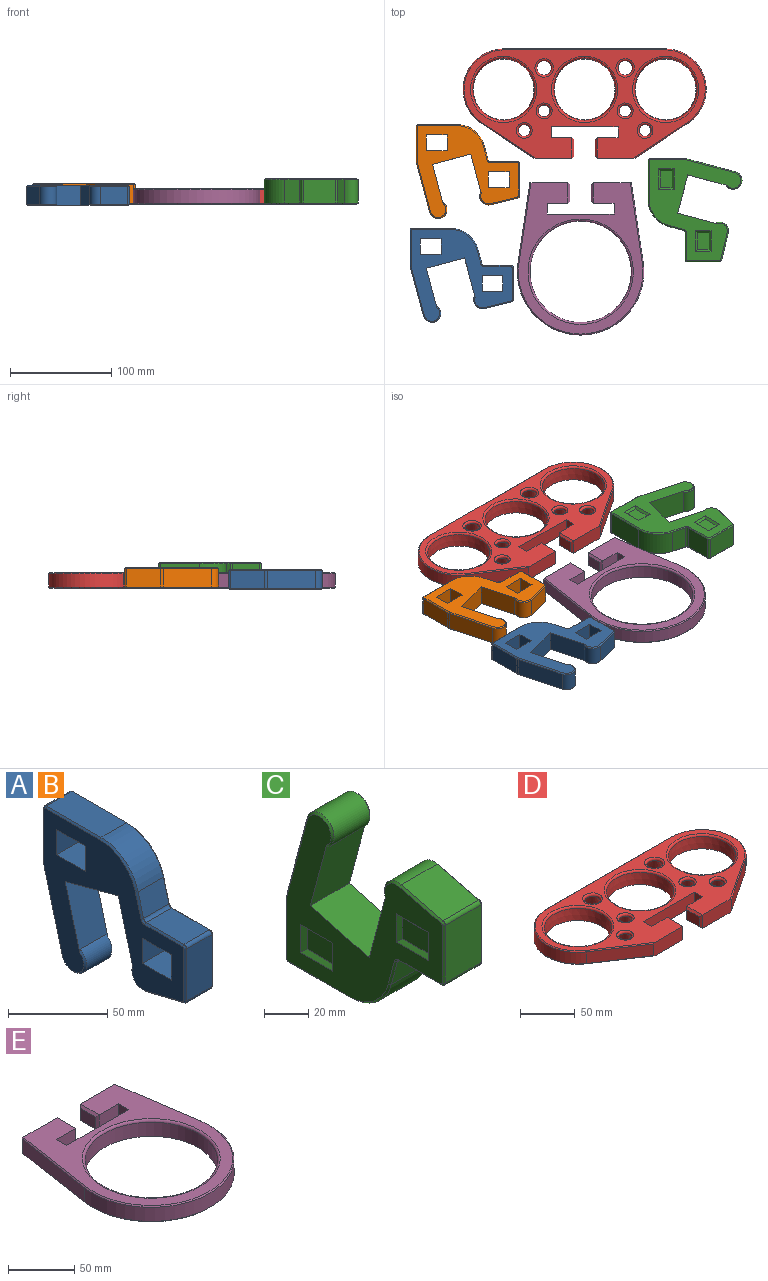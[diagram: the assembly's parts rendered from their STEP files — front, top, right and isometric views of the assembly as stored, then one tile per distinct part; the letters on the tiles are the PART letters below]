
ASSEMBLY  parts=5 mates=3
PART A: 58 faces, bbox 20x101.8x92.6 mm
  f0: plane 99.77x90.57mm, normal (1,0,0), area 3782.3mm2, adj f1,f2,f3,f4,f5,f15,f16,f17
  f1: plane 20x15.6mm, normal (0,-1,0), area 312mm2, adj f0,f14,f15,f16
  f2: plane 20x15.6mm, normal (0,-1,0), area 312mm2, adj f0,f14,f21,f22
  f3: plane 38.64x20mm, normal (0,0.97,-0.26), area 770.8mm2, adj f0,f4,f14,f19,f42,f57
  f4: plane 37.77x20mm, normal (0,-0.26,-0.97), area 782mm2, adj f0,f3,f5,f14
  f5: plane 38.64x20mm, normal (0,-0.97,0.26), area 770.8mm2, adj f0,f4,f6,f14,f28,f43
  f6: cylinder r=8.75mm len=18mm, axis (-1,0,0), area 616.9mm2, adj f5,f7,f28,f43
  f7: plane 47.9x18mm, normal (0,0.97,-0.26), area 892.6mm2, adj f6,f8,f29,f44
  f8: cylinder r=10mm len=18mm, axis (-1,0,0), area 47.1mm2, adj f7,f9,f30,f45
  f9: plane 33.6x18mm, normal (0,1,0), area 604.8mm2, adj f8,f24,f31,f46
  f10: plane 38.63x18mm, normal (0,0,1), area 695.3mm2, adj f11,f24,f33,f48
  f11: cylinder r=27.39mm len=26.46mm, axis (-1,0,0), area 645.5mm2, adj f10,f12,f34,f49
  f12: plane 18x14.63mm, normal (0,-0.97,0.26), area 272.7mm2, adj f11,f25,f35,f50
  f13: plane 26.83x18mm, normal (0,0,1), area 482.9mm2, adj f25,f26,f37,f52
  f14: plane 99.77x90.57mm, normal (-1,0,0), area 3782.3mm2, adj f1,f2,f3,f4,f5,f15,f16,f17
  f15: plane 20.6x20mm, normal (0,0,1), area 412mm2, adj f0,f1,f14,f17
  f16: plane 20.6x20mm, normal (0,0,-1), area 412mm2, adj f0,f1,f14,f17
  f17: plane 20x15.6mm, normal (0,1,0), area 312mm2, adj f0,f14,f15,f16
  f18: plane 32.03x18mm, normal (0,-1,0), area 576.6mm2, adj f26,f27,f39,f54
  f19: cylinder r=8.75mm len=18mm, axis (-1,0,0), area 366.3mm2, adj f3,f20,f42,f57
  f20: plane 26.69x18mm, normal (0,-0.24,-0.97), area 494.7mm2, adj f19,f27,f41,f56
  f21: plane 20.6x20mm, normal (0,0,1), area 412mm2, adj f0,f2,f14,f23
  f22: plane 20.6x20mm, normal (0,0,-1), area 412mm2, adj f0,f2,f14,f23
  f23: plane 20x15.6mm, normal (0,1,0), area 312mm2, adj f0,f14,f21,f22
  f24: cylinder r=2mm len=18mm, axis (-1,0,0), area 56.5mm2, adj f9,f10,f32,f47
  f25: cylinder r=2mm len=18mm, axis (1,0,0), area 47.1mm2, adj f12,f13,f36,f51
  f26: cylinder r=2mm len=18mm, axis (-1,0,0), area 56.5mm2, adj f13,f18,f38,f53
  f27: cylinder r=2mm len=18mm, axis (-1,0,0), area 47.9mm2, adj f18,f20,f40,f55
  f28: cone r=8.75mm half-angle=45deg, axis (1,0,0), area 44.9mm2, adj f5,f6,f14,f29
  f29: plane 48.16x13.8mm, normal (-0.71,0.68,-0.18), area 70.1mm2, adj f7,f14,f28,f30
  f30: cone r=10mm half-angle=45deg, axis (1,0,0), area 3.5mm2, adj f8,f14,f29,f31
  f31: plane 33.6x1mm, normal (-0.71,0.71,0), area 47.5mm2, adj f9,f14,f30,f32
  f32: cone r=1mm half-angle=45deg, axis (1,0,0), area 3.3mm2, adj f14,f24,f31,f33
  f33: plane 38.63x1mm, normal (-0.71,0,0.71), area 54.6mm2, adj f10,f14,f32,f34
  f34: cone r=27.39mm half-angle=45deg, axis (1,0,0), area 49.8mm2, adj f11,f14,f33,f35
  f35: plane 14.89x4.89mm, normal (-0.71,-0.68,0.18), area 21.4mm2, adj f12,f14,f34,f36
  f36: cone r=3mm half-angle=45deg, axis (-1,0,0), area 4.6mm2, adj f14,f25,f35,f37
  f37: plane 26.83x1mm, normal (-0.71,0,0.71), area 37.9mm2, adj f13,f14,f36,f38
  f38: cone r=1mm half-angle=45deg, axis (1,0,0), area 3.3mm2, adj f14,f26,f37,f39
  f39: plane 32.03x1mm, normal (-0.71,-0.71,0), area 45.3mm2, adj f14,f18,f38,f40
  f40: cone r=1mm half-angle=45deg, axis (1,0,0), area 2.8mm2, adj f14,f27,f39,f41
  f41: plane 26.93x7.54mm, normal (-0.71,-0.17,-0.69), area 38.9mm2, adj f14,f20,f40,f42
  f42: cone r=8.75mm half-angle=45deg, axis (1,0,0), area 26.4mm2, adj f3,f14,f19,f41
  f43: cone r=7.75mm half-angle=45deg, axis (-1,0,0), area 44.9mm2, adj f0,f5,f6,f44
  f44: plane 48.16x13.8mm, normal (0.71,0.68,-0.18), area 70.1mm2, adj f0,f7,f43,f45
  f45: cone r=9mm half-angle=45deg, axis (-1,0,0), area 3.5mm2, adj f0,f8,f44,f46
  f46: plane 33.6x1mm, normal (0.71,0.71,0), area 47.5mm2, adj f0,f9,f45,f47
  f47: cone r=1mm half-angle=45deg, axis (-1,0,0), area 3.3mm2, adj f0,f24,f46,f48
  f48: plane 38.63x1mm, normal (0.71,0,0.71), area 54.6mm2, adj f0,f10,f47,f49
  f49: cone r=26.39mm half-angle=45deg, axis (-1,0,0), area 49.8mm2, adj f0,f11,f48,f50
  f50: plane 14.89x4.89mm, normal (0.71,-0.68,0.18), area 21.4mm2, adj f0,f12,f49,f51
  f51: cone r=3mm half-angle=45deg, axis (1,0,0), area 4.6mm2, adj f0,f25,f50,f52
  f52: plane 26.83x1mm, normal (0.71,0,0.71), area 37.9mm2, adj f0,f13,f51,f53
  f53: cone r=1mm half-angle=45deg, axis (-1,0,0), area 3.3mm2, adj f0,f26,f52,f54
  f54: plane 32.03x1mm, normal (0.71,-0.71,0), area 45.3mm2, adj f0,f18,f53,f55
  f55: cone r=1mm half-angle=45deg, axis (-1,0,0), area 2.8mm2, adj f0,f27,f54,f56
  f56: plane 26.93x7.54mm, normal (0.71,-0.17,-0.69), area 38.9mm2, adj f0,f20,f55,f57
  f57: cone r=7.75mm half-angle=45deg, axis (-1,0,0), area 26.4mm2, adj f0,f3,f19,f56
PART B: same geometry as A
PART C: 70 faces, bbox 25x101.8x92.6 mm
  f0: plane 99.77x90.57mm, normal (-1,0,0), area 3782.3mm2, adj f1,f2,f8,f20,f21,f22,f23,f24
  f1: plane 37.77x25mm, normal (0,-0.26,0.97), area 977.5mm2, adj f0,f2,f8,f12
  f2: plane 38.64x25mm, normal (0,0.97,0.26), area 963.1mm2, adj f0,f1,f3,f12,f54,f69
  f3: cylinder r=8.75mm len=23mm, axis (1,0,0), area 468mm2, adj f2,f4,f54,f69
  f4: plane 26.69x23mm, normal (0,-0.24,0.97), area 632.1mm2, adj f3,f36,f53,f68
  f5: plane 32.03x23mm, normal (0,-1,0), area 736.8mm2, adj f36,f37,f51,f66
  f6: plane 26.83x23mm, normal (0,0,-1), area 617.1mm2, adj f37,f38,f49,f64
  f7: plane 23x14.63mm, normal (0,-0.97,-0.26), area 348.4mm2, adj f9,f38,f47,f62
  f8: plane 38.64x25mm, normal (0,-0.97,-0.26), area 963.1mm2, adj f0,f1,f11,f12,f40,f55
  f9: cylinder r=27.39mm len=26.46mm, axis (1,0,0), area 824.7mm2, adj f7,f10,f46,f61
  f10: plane 38.63x23mm, normal (0,0,-1), area 888.4mm2, adj f9,f39,f45,f60
  f11: cylinder r=8.75mm len=23mm, axis (1,0,0), area 788.3mm2, adj f8,f13,f40,f55
  f12: plane 99.77x90.57mm, normal (1,0,0), area 3782.3mm2, adj f1,f2,f8,f28,f29,f30,f31,f32
  f13: plane 47.9x23mm, normal (0,0.97,0.26), area 1140.6mm2, adj f11,f15,f41,f56
  f14: plane 33.6x23mm, normal (0,1,0), area 772.8mm2, adj f15,f39,f43,f58
  f15: cylinder r=10mm len=23mm, axis (1,0,0), area 60.2mm2, adj f13,f14,f42,f57
  f16: plane 16.6x11.6mm, normal (-1,0,0), area 192.6mm2, adj f24,f25,f26,f27
  f17: plane 16.6x11.6mm, normal (1,0,0), area 192.6mm2, adj f32,f33,f34,f35
  f18: plane 16.6x11.6mm, normal (-1,0,0), area 192.6mm2, adj f20,f21,f22,f23
  f19: plane 16.6x11.6mm, normal (1,0,0), area 192.6mm2, adj f28,f29,f30,f31
  f20: plane 15.6x2mm, normal (-0.71,0.71,0), area 38.5mm2, adj f0,f18,f21,f22
  f21: plane 20.6x2mm, normal (-0.71,0,0.71), area 52.6mm2, adj f0,f18,f20,f23
  f22: plane 20.6x2mm, normal (-0.71,0,-0.71), area 52.6mm2, adj f0,f18,f20,f23
  f23: plane 15.6x2mm, normal (-0.71,-0.71,0), area 38.5mm2, adj f0,f18,f21,f22
  f24: plane 15.6x2mm, normal (-0.71,0.71,0), area 38.5mm2, adj f0,f16,f25,f26
  f25: plane 20.6x2mm, normal (-0.71,0,0.71), area 52.6mm2, adj f0,f16,f24,f27
  f26: plane 20.6x2mm, normal (-0.71,0,-0.71), area 52.6mm2, adj f0,f16,f24,f27
  f27: plane 15.6x2mm, normal (-0.71,-0.71,0), area 38.5mm2, adj f0,f16,f25,f26
  f28: plane 15.6x2mm, normal (0.71,0.71,0), area 38.5mm2, adj f12,f19,f29,f30
  f29: plane 20.6x2mm, normal (0.71,0,0.71), area 52.6mm2, adj f12,f19,f28,f31
  f30: plane 20.6x2mm, normal (0.71,0,-0.71), area 52.6mm2, adj f12,f19,f28,f31
  f31: plane 15.6x2mm, normal (0.71,-0.71,0), area 38.5mm2, adj f12,f19,f29,f30
  f32: plane 15.6x2mm, normal (0.71,0.71,0), area 38.5mm2, adj f12,f17,f33,f34
  f33: plane 20.6x2mm, normal (0.71,0,0.71), area 52.6mm2, adj f12,f17,f32,f35
  f34: plane 20.6x2mm, normal (0.71,0,-0.71), area 52.6mm2, adj f12,f17,f32,f35
  f35: plane 15.6x2mm, normal (0.71,-0.71,0), area 38.5mm2, adj f12,f17,f33,f34
  f36: cylinder r=2mm len=23mm, axis (1,0,0), area 61.2mm2, adj f4,f5,f52,f67
  f37: cylinder r=2mm len=23mm, axis (1,0,0), area 72.3mm2, adj f5,f6,f50,f65
  f38: cylinder r=2mm len=23mm, axis (-1,0,0), area 60.2mm2, adj f6,f7,f48,f63
  f39: cylinder r=2mm len=23mm, axis (1,0,0), area 72.3mm2, adj f10,f14,f44,f59
  f40: cone r=7.75mm half-angle=45deg, axis (1,0,0), area 44.9mm2, adj f0,f8,f11,f41
  f41: plane 48.16x13.8mm, normal (-0.71,0.68,0.18), area 70.1mm2, adj f0,f13,f40,f42
  f42: cone r=9mm half-angle=45deg, axis (1,0,0), area 3.5mm2, adj f0,f15,f41,f43
  f43: plane 33.6x1mm, normal (-0.71,0.71,0), area 47.5mm2, adj f0,f14,f42,f44
  f44: cone r=1mm half-angle=45deg, axis (1,0,0), area 3.3mm2, adj f0,f39,f43,f45
  f45: plane 38.63x1mm, normal (-0.71,0,-0.71), area 54.6mm2, adj f0,f10,f44,f46
  f46: cone r=26.39mm half-angle=45deg, axis (1,0,0), area 49.8mm2, adj f0,f9,f45,f47
  f47: plane 14.89x4.89mm, normal (-0.71,-0.68,-0.18), area 21.4mm2, adj f0,f7,f46,f48
  f48: cone r=3mm half-angle=45deg, axis (-1,0,0), area 4.6mm2, adj f0,f38,f47,f49
  f49: plane 26.83x1mm, normal (-0.71,0,-0.71), area 37.9mm2, adj f0,f6,f48,f50
  f50: cone r=1mm half-angle=45deg, axis (1,0,0), area 3.3mm2, adj f0,f37,f49,f51
  f51: plane 32.03x1mm, normal (-0.71,-0.71,0), area 45.3mm2, adj f0,f5,f50,f52
  f52: cone r=1mm half-angle=45deg, axis (1,0,0), area 2.8mm2, adj f0,f36,f51,f53
  f53: plane 26.93x7.54mm, normal (-0.71,-0.17,0.69), area 38.9mm2, adj f0,f4,f52,f54
  f54: cone r=7.75mm half-angle=45deg, axis (1,0,0), area 26.4mm2, adj f0,f2,f3,f53
  f55: cone r=8.75mm half-angle=45deg, axis (-1,0,0), area 44.9mm2, adj f8,f11,f12,f56
  f56: plane 48.16x13.8mm, normal (0.71,0.68,0.18), area 70.1mm2, adj f12,f13,f55,f57
  f57: cone r=10mm half-angle=45deg, axis (-1,0,0), area 3.5mm2, adj f12,f15,f56,f58
  f58: plane 33.6x1mm, normal (0.71,0.71,0), area 47.5mm2, adj f12,f14,f57,f59
  f59: cone r=1mm half-angle=45deg, axis (-1,0,0), area 3.3mm2, adj f12,f39,f58,f60
  f60: plane 38.63x1mm, normal (0.71,0,-0.71), area 54.6mm2, adj f10,f12,f59,f61
  f61: cone r=27.39mm half-angle=45deg, axis (-1,0,0), area 49.8mm2, adj f9,f12,f60,f62
  f62: plane 14.89x4.89mm, normal (0.71,-0.68,-0.18), area 21.4mm2, adj f7,f12,f61,f63
  f63: cone r=3mm half-angle=45deg, axis (1,0,0), area 4.6mm2, adj f12,f38,f62,f64
  f64: plane 26.83x1mm, normal (0.71,0,-0.71), area 37.9mm2, adj f6,f12,f63,f65
  f65: cone r=1mm half-angle=45deg, axis (-1,0,0), area 3.3mm2, adj f12,f37,f64,f66
  f66: plane 32.03x1mm, normal (0.71,-0.71,0), area 45.3mm2, adj f5,f12,f65,f67
  f67: cone r=1mm half-angle=45deg, axis (-1,0,0), area 2.8mm2, adj f12,f36,f66,f68
  f68: plane 26.93x7.54mm, normal (0.71,-0.17,0.69), area 38.9mm2, adj f4,f12,f67,f69
  f69: cone r=8.75mm half-angle=45deg, axis (-1,0,0), area 26.4mm2, adj f2,f3,f12,f68
PART D: 52 faces, bbox 240x107.8x15 mm
  f0: plane 238x106.8mm, normal (0,0,1), area 8736.8mm2, adj f2,f3,f4,f5,f6,f8,f10,f28
  f1: plane 16x11mm, normal (1,0,0), area 176mm2, adj f25,f26,f27,f28
  f2: plane 20.5x15mm, normal (0,1,0), area 307.5mm2, adj f0,f3,f13,f26
  f3: plane 15x10.8mm, normal (1,0,0), area 162mm2, adj f0,f2,f4,f13
  f4: plane 66x15mm, normal (0,-1,0), area 990mm2, adj f0,f3,f5,f13
  f5: plane 15x10.8mm, normal (-1,0,0), area 162mm2, adj f0,f4,f6,f13
  f6: plane 20.5x15mm, normal (0,1,0), area 307.5mm2, adj f0,f5,f13,f30
  f7: plane 16x11mm, normal (-1,0,0), area 176mm2, adj f29,f30,f31,f32
  f8: plane 37.5x15mm, normal (0,-1,0), area 560.7mm2, adj f0,f9,f13,f31,f46,f47
  f9: plane 52.07x34.44mm, normal (0.55,-0.83,0), area 811.5mm2, adj f8,f11,f46,f47
  f10: plane 37.5x15mm, normal (0,-1,0), area 560.7mm2, adj f0,f12,f13,f27,f42,f51
  f11: cylinder r=40mm len=73.36mm, axis (0,0,-1), area 1329.8mm2, adj f9,f23,f45,f48
  f12: plane 52.07x34.44mm, normal (-0.55,-0.83,0), area 811.5mm2, adj f10,f24,f42,f51
  f13: plane 238x106.8mm, normal (0,0,-1), area 9382.8mm2, adj f2,f3,f4,f5,f6,f8,f10,f14
  f14: cone r=30mm half-angle=3deg, axis (0,0,1), area 2501.9mm2, adj f13,f41
  f15: cone r=30mm half-angle=3deg, axis (0,0,1), area 2501.9mm2, adj f13,f40
  f16: cone r=30mm half-angle=3deg, axis (0,0,1), area 2501.9mm2, adj f13,f39
  f17: cone r=6.25mm half-angle=20deg, axis (0,0,-1), area 779.7mm2, adj f13,f38
  f18: cone r=5mm half-angle=20deg, axis (0,0,-1), area 676.8mm2, adj f13,f33
  f19: cone r=5mm half-angle=20deg, axis (0,0,-1), area 676.8mm2, adj f13,f37
  f20: cone r=5mm half-angle=20deg, axis (0,0,-1), area 676.8mm2, adj f13,f34
  f21: cone r=5mm half-angle=20deg, axis (0,0,-1), area 676.8mm2, adj f13,f36
  f22: cone r=6.25mm half-angle=20deg, axis (0,0,-1), area 779.7mm2, adj f13,f35
  f23: plane 160x13mm, normal (0,1,0), area 2080mm2, adj f11,f24,f44,f49
  f24: cylinder r=40mm len=73.36mm, axis (0,0,-1), area 1329.8mm2, adj f12,f23,f43,f50
  f25: plane 20x2mm, normal (0.71,0,-0.71), area 50.9mm2, adj f1,f13,f26,f27
  f26: plane 15x2mm, normal (0.71,0.71,0), area 36.8mm2, adj f1,f2,f25,f28
  f27: plane 15x2mm, normal (0.71,-0.71,0), area 36.8mm2, adj f1,f10,f25,f28
  f28: plane 20x2mm, normal (0.71,0,0.71), area 50.9mm2, adj f0,f1,f26,f27
  f29: plane 20x2mm, normal (-0.71,0,-0.71), area 50.9mm2, adj f7,f13,f30,f31
  f30: plane 15x2mm, normal (-0.71,0.71,0), area 36.8mm2, adj f6,f7,f29,f32
  f31: plane 15x2mm, normal (-0.71,-0.71,0), area 36.8mm2, adj f7,f8,f29,f32
  f32: plane 20x2mm, normal (-0.71,0,0.71), area 50.9mm2, adj f0,f7,f30,f31
  f33: torus R=7.86mm, axis (0,0,1), area 155.8mm2, adj f0,f18
  f34: torus R=7.86mm, axis (0,0,1), area 155.8mm2, adj f0,f20
  f35: torus R=9.11mm, axis (0,0,1), area 186mm2, adj f0,f22
  f36: torus R=7.86mm, axis (0,0,1), area 155.8mm2, adj f0,f21
  f37: torus R=7.86mm, axis (0,0,1), area 155.8mm2, adj f0,f19
  f38: torus R=9.11mm, axis (0,0,1), area 186mm2, adj f0,f17
  f39: torus R=32.68mm, axis (0,0,1), area 599.8mm2, adj f0,f16
  f40: torus R=32.68mm, axis (0,0,1), area 599.8mm2, adj f0,f15
  f41: torus R=32.68mm, axis (0,0,1), area 599.8mm2, adj f0,f14
  f42: plane 53.88x35.27mm, normal (-0.39,-0.59,0.71), area 89.4mm2, adj f0,f10,f12,f43
  f43: cone r=39mm half-angle=45deg, axis (0,0,-1), area 142.9mm2, adj f0,f24,f42,f44
  f44: plane 160x1mm, normal (0,0.71,0.71), area 226.3mm2, adj f0,f23,f43,f45
  f45: cone r=40mm half-angle=45deg, axis (0,0,-1), area 142.9mm2, adj f0,f11,f44,f46
  f46: plane 53.88x35.27mm, normal (0.39,-0.59,0.71), area 89.4mm2, adj f0,f8,f9,f45
  f47: plane 53.88x35.27mm, normal (0.39,-0.59,-0.71), area 89.4mm2, adj f8,f9,f13,f48
  f48: cone r=39mm half-angle=45deg, axis (0,0,1), area 142.9mm2, adj f11,f13,f47,f49
  f49: plane 160x1mm, normal (0,0.71,-0.71), area 226.3mm2, adj f13,f23,f48,f50
  f50: cone r=40mm half-angle=45deg, axis (0,0,1), area 142.9mm2, adj f13,f24,f49,f51
  f51: plane 53.88x35.27mm, normal (-0.39,-0.59,-0.71), area 89.4mm2, adj f10,f12,f13,f50
PART E: 30 faces, bbox 125x150.3x15 mm
  f0: plane 149.3x123mm, normal (0,0,1), area 5990.9mm2, adj f1,f5,f7,f8,f9,f11,f13,f18
  f1: plane 37.5x15mm, normal (0,1,0), area 561.5mm2, adj f0,f2,f10,f17,f26,f29
  f2: plane 78.51x13mm, normal (-0.99,0.15,0), area 1032.1mm2, adj f1,f3,f26,f29
  f3: cylinder r=62.5mm len=125mm, axis (0,0,-1), area 2795.1mm2, adj f2,f4,f25,f28
  f4: plane 78.51x13mm, normal (0.99,0.15,0), area 1032.1mm2, adj f3,f5,f24,f27
  f5: plane 37.5x15mm, normal (0,1,0), area 561.5mm2, adj f0,f4,f10,f21,f24,f27
  f6: plane 16x11mm, normal (-1,0,0), area 176mm2, adj f19,f20,f21,f22
  f7: plane 20.5x15mm, normal (0,-1,0), area 307.5mm2, adj f0,f8,f10,f20
  f8: plane 15x10.8mm, normal (-1,0,0), area 162mm2, adj f0,f7,f9,f10
  f9: plane 66x15mm, normal (0,1,0), area 990mm2, adj f0,f8,f10,f11
  f10: plane 149.3x123mm, normal (0,0,-1), area 6631.8mm2, adj f1,f5,f7,f8,f9,f11,f13,f14
  f11: plane 15x10.8mm, normal (1,0,0), area 162mm2, adj f0,f9,f10,f13
  f12: plane 16x11mm, normal (1,0,0), area 176mm2, adj f15,f16,f17,f18
  f13: plane 20.5x15mm, normal (0,-1,0), area 307.5mm2, adj f0,f10,f11,f16
  f14: cylinder r=50mm len=100mm, axis (0,0,-1), area 4084.1mm2, adj f10,f23
  f15: plane 20x2mm, normal (0.71,0,-0.71), area 50.9mm2, adj f10,f12,f16,f17
  f16: plane 15x2mm, normal (0.71,-0.71,0), area 36.8mm2, adj f12,f13,f15,f18
  f17: plane 15x2mm, normal (0.71,0.71,0), area 36.8mm2, adj f1,f12,f15,f18
  f18: plane 20x2mm, normal (0.71,0,0.71), area 50.9mm2, adj f0,f12,f16,f17
  f19: plane 20x2mm, normal (-0.71,0,-0.71), area 50.9mm2, adj f6,f10,f20,f21
  f20: plane 15x2mm, normal (-0.71,-0.71,0), area 36.8mm2, adj f6,f7,f19,f22
  f21: plane 15x2mm, normal (-0.71,0.71,0), area 36.8mm2, adj f5,f6,f19,f22
  f22: plane 20x2mm, normal (-0.71,0,0.71), area 50.9mm2, adj f0,f6,f20,f21
  f23: torus R=52mm, axis (0,0,1), area 1001.3mm2, adj f0,f14
  f24: plane 78.66x12.82mm, normal (0.7,0.11,-0.71), area 112.4mm2, adj f4,f5,f10,f25
  f25: cone r=62.5mm half-angle=45deg, axis (0,0,1), area 301.6mm2, adj f3,f10,f24,f26
  f26: plane 78.66x12.82mm, normal (-0.7,0.11,-0.71), area 112.4mm2, adj f1,f2,f10,f25
  f27: plane 78.66x12.82mm, normal (0.7,0.11,0.71), area 112.4mm2, adj f0,f4,f5,f28
  f28: cone r=61.5mm half-angle=45deg, axis (0,0,-1), area 301.6mm2, adj f0,f3,f27,f29
  f29: plane 78.66x12.82mm, normal (-0.7,0.11,0.71), area 112.4mm2, adj f0,f1,f2,f28
PLACE A rot(axis=(-0.58,0.58,0.58),120deg) t=(-128.34,-129.52,22.5)mm
PLACE B rot(axis=(-0.58,0.58,0.58),120deg) t=(-122.24,-27.03,23.74)mm
PLACE C rot(axis=(0,1,0),90deg) t=(-26.24,-47.52,3.74)mm
PLACE D t=(3.96,-16.79,-36.42)mm
PLACE E at identity fixed
MATE planar D.f13 <-> E.f10  axis (0,0,-1) through (52.15,-7.02,-8.76)mm
MATE planar B.f0 <-> E.f10  axis (0,0,-1) through (-117.74,-14.16,-8.76)mm
MATE planar C.f12 <-> E.f10  axis (0,0,-1) through (76.72,-38.06,-8.76)mm
